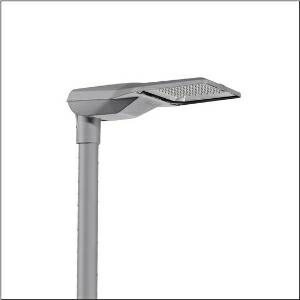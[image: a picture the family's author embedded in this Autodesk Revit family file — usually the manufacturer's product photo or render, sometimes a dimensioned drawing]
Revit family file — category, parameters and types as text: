
# Revit family: streetlight_sl_21_midi___st1_0a_5xe7d43a08mb_b8fa
name_source: partatom
category: Lighting Fixtures
units: mm (PartAtom-declared; Revit-internal decimal feet)

## family parameters
Cut with Voids When Loaded = No
Host = Face
Light Source = No
Part Type = Normal
Room Calculation Point = No
Round Connector Dimension = Use Diameter
Shared = No

## types (1)
- --- (1 x LED, 20180 lm, 147 W, 4000K)
    Apparent Load = 147 VA
    CIE Flux Codes = 37 72 97 100 100
    Color Rendering = 70
    Color Temperature = 4000K
    Default Elevation = 1800 mm
    Description = Streetlight SL 21 midi, mast luminaire, primary light control with lens, of PMMA, primary optical cover: cover, of toughened safety glass, transparent, light distribution: ST1.0a, light emission: direct distribution, primary light characteristic: asymmetric, installation type: post-top, side-entry, LED, 3G 1.5mm², High Power LED, rated luminous flux: 20.180lm, luminous efficacy: 137lm/W, light colour: 740, colour temperature: 4000K, control gear: Easy, control: overheat protection, constant luminous flux control, time-dependent luminous flux control, flexible luminous flux parameterisation, mains connection: 220..240V, AC, 50/60Hz, connection cable pre-assembled, cable length: 12,5m, wiring characteristics: H07RN-F, start of lifetime: 147W, end of service life: 155W, reduction: 64W, luminaire housing, of diecast aluminium, powder-coated, Siteco® metallic grey (DB 702S), corrosivity category C5 mid according to DIN EN ISO 12944, please order mast flange separately, inclination adjustable: 0°, 5°, 10°, 15°, sealing non-destructively replaceable, multi-level sealing system, length: 644mm, width: 335mm, height: 110mm, mast flange for spigot size: 42mm (side-entry): 5XC10008XM4, 60/48mm (side-entry/post-top): 5XC10108XM2, 76/60mm (side-entry/post-top): 5XC10108XM1, mounting height: 4..8m, protection rating (complete): IP66, insulation class (complete): insulation class II (safety insulation), certification: CE, ENEC, ENEC+, VDE, impact resistance: IK10, permissible operating ambient temperature for outdoor applications: -40..+50°C, standard-compliant lighting for roads and squares, packaging unit: 1 piece

Light Distribution: ST1.0a
    Height = 111 mm
    Lamp = 1 x LED
    Lamp Light Flux = 20180 lm
    Lamp Power = 147 W
    Lamp count = 1
    Length = 644 mm
    Luminous efficacy = 137 lm/W
    Manufacturer = Siteco
    ModVariant = No
    Model = 5XE7D43A08MB
    Number of Poles = 1
    OnlyDefault = Yes
    Power Factor = 1
    Product Name = Streetlight SL 21 midi | ST1.0a
    Product group = mast luminaire | pylon top
    ProductGroupID = 6100
    Protection Class = Protection class II
    Protection Degree = IP 66
    RLX_Detail_Level = 1
    RLX_Emergency_Light_Flux = 0 lm
    RLX_Emergency_Type = 0
    RLX_Emergency_Type_DB = No
    RlxData = <blob elided: 26777 chars, md5=78b7a01b>
    Socket = socket
    Standby Power = 0 W
    System Light Flux = 20180 lm
    System Power = 147 W
    Type Comments = factory setting: luminous flux: 100 % | Output Level: 100 % | 750 mA
    Type Image = l_1004298.jpg
    URL = http://relux.com
    VarID = @adj_210293
    Voltage = 0 V
    Weight = 0.00 kg
    Width = 336 mm

## geometry (parser evidence)
native form markers: Blend x4, Sweep x12
no freeform markers — native parametric forms only
